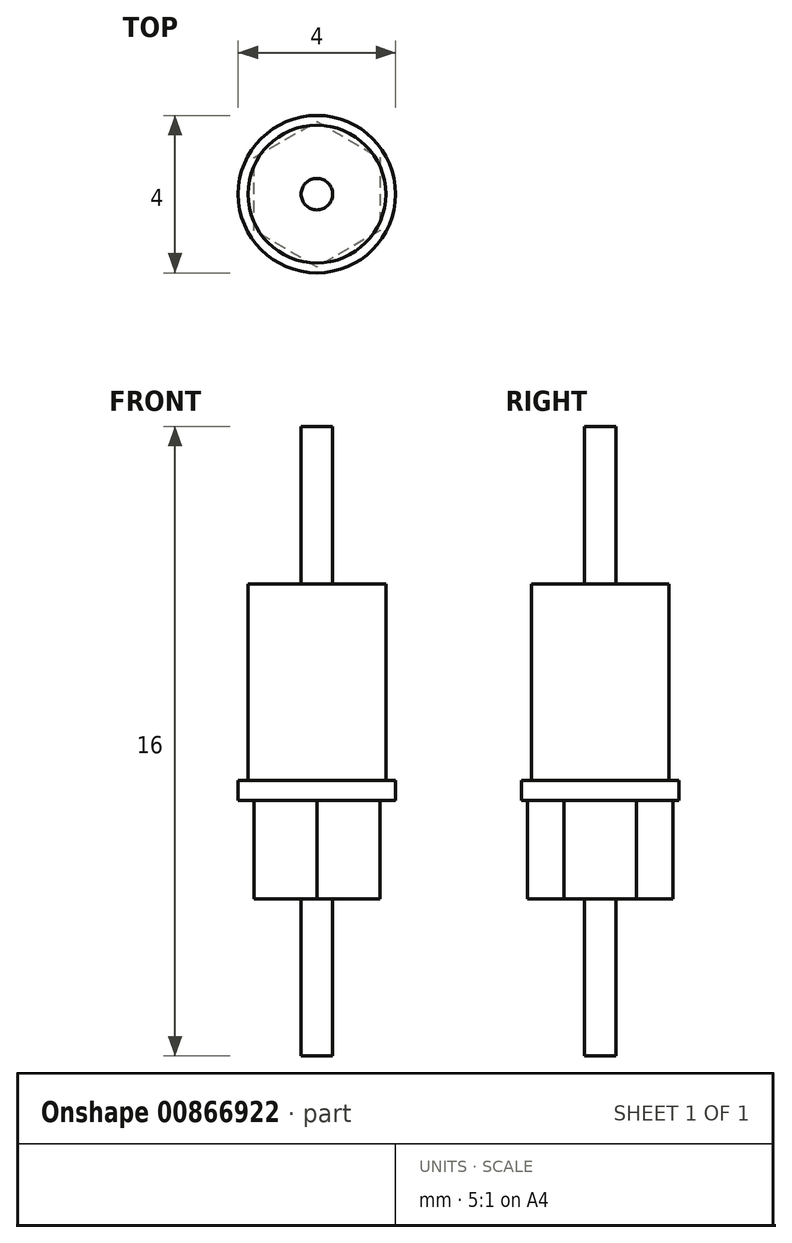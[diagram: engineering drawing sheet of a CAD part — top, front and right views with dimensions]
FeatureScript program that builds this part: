
annotation { "Feature Type Name" : "Feature", "Feature Type Description" : "" }
export const myFeature = defineFeature(function(context is Context, id is Id, definition is map)
    precondition{}
    {
        {
            var Q0;
            Q0=qCreatedBy(makeId("Top.planeOp"),FACE);
            var sketch = newSketch(context, id + "F0", { "sketchPlane" : qUnion([Q0])});
            skCircle(sketch, "E0", {"center": v(0, 0) * mm, "radius": 0.4 * mm});
            skSolve(sketch);
        }
        {
            var Q0;
            Q0=makeQuery(id+"F0.imprint","IMPRINT",FACE,{"disambiguationData":[TD([[makeQuery(id+"F0.imprint","IMPRINT",EDGE,{"derivedFrom":sQuery(id+"F0.wireOp",EDGE,"E0")}),1.0]])]});
            extrude(context, id + "F1", {"entities" : qUnion([Q0]), "depth" : 4 * mm, "offsetDistance" : 25 * mm});
        }
        {
            var Q0;
            Q0=makeQuery(id+"F1.opExtrude","CAP_FACE",FACE,{"disambiguationData":[OSD([sQuery(id+"F0.wireOp",EDGE,"E0")])],"isStart":false});
            var sketch = newSketch(context, id + "F2", { "sketchPlane" : qUnion([Q0])});
            skCircle(sketch, "E1.cCircle", {"center": v(0, 0) * mm, "radius": 1.6 * mm, "construction": true});
            skLineSegment(sketch, "E1.0", {"start": v(1.6, 0.92) * mm, "end": v(1.6, -0.92) * mm});
            skLineSegment(sketch, "E1.1", {"start": v(1.6, -0.92) * mm, "end": v(0, -1.85) * mm});
            skLineSegment(sketch, "E1.2", {"start": v(0, -1.85) * mm, "end": v(-1.6, -0.92) * mm});
            skLineSegment(sketch, "E1.3", {"start": v(-1.6, -0.92) * mm, "end": v(-1.6, 0.92) * mm});
            skLineSegment(sketch, "E1.4", {"start": v(-1.6, 0.92) * mm, "end": v(0, 1.85) * mm});
            skLineSegment(sketch, "E1.5", {"start": v(0, 1.85) * mm, "end": v(1.6, 0.92) * mm});
            skPoint(sketch, "E1.0.midPoint", {"position": v(1.6, 0) * mm});
            skSolve(sketch);
        }
        {
            var Q0;
            Q0=makeQuery(id+"F2.imprint","IMPRINT",FACE,{"disambiguationData":[TD([[makeQuery(id+"F2.imprint","IMPRINT",EDGE,{"derivedFrom":sQuery(id+"F2.wireOp",EDGE,"E1.0")}),-1.0]])]});
            var Q1;
            Q1=makeQuery(id+"F2.imprint","IMPRINT",FACE,{"disambiguationData":[TD([[makeQuery(id+"F2.imprint","IMPRINT",EDGE,{"derivedFrom":makeQuery(id+"F1.opExtrude","CAP_EDGE",EDGE,{"disambiguationData":[OSD([sQuery(id+"F0.wireOp",EDGE,"E0")])],"isStart":false})}),1.0]])]});
            extrude(context, id + "F3", {"entities" : qUnion([Q0, Q1]), "operationType" : NewBodyOperationType.ADD, "depth" : 2.5 * mm, "offsetDistance" : 25 * mm});
        }
        {
            var Q0;
            Q0=makeQuery(id+"F3.opExtrude","CAP_FACE",FACE,{"disambiguationData":[OSD([sQuery(id+"F0.wireOp",EDGE,"E0"),sQuery(id+"F2.wireOp",EDGE,"E1.0"),sQuery(id+"F2.wireOp",EDGE,"E1.1"),sQuery(id+"F2.wireOp",EDGE,"E1.2"),sQuery(id+"F2.wireOp",EDGE,"E1.3"),sQuery(id+"F2.wireOp",EDGE,"E1.4"),sQuery(id+"F2.wireOp",EDGE,"E1.5")])],"isStart":false});
            var sketch = newSketch(context, id + "F4", { "sketchPlane" : qUnion([Q0])});
            skCircle(sketch, "E2", {"center": v(0, 0) * mm, "radius": 2 * mm});
            skSolve(sketch);
        }
        {
            var Q0;
            Q0=makeQuery(id+"F4.imprint","IMPRINT",FACE,{"disambiguationData":[TD([[makeQuery(id+"F4.imprint","IMPRINT",EDGE,{"derivedFrom":sQuery(id+"F4.wireOp",EDGE,"E2")}),1.0]])]});
            var Q1;
            Q1=makeQuery(id+"F4.imprint","IMPRINT",FACE,{"disambiguationData":[TD([[makeQuery(id+"F4.imprint","IMPRINT",EDGE,{"derivedFrom":makeQuery(id+"F3.opExtrude","CAP_EDGE",EDGE,{"disambiguationData":[OSD([sQuery(id+"F2.wireOp",EDGE,"E1.0")])],"isStart":false})}),-1.0]])]});
            extrude(context, id + "F5", {"entities" : qUnion([Q0, Q1]), "operationType" : NewBodyOperationType.ADD, "depth" : 0.5 * mm, "offsetDistance" : 25 * mm});
        }
        {
            var Q0;
            Q0=makeQuery(id+"F5.opExtrude","CAP_FACE",FACE,{"disambiguationData":[OSD([sQuery(id+"F4.wireOp",EDGE,"E2")])],"isStart":false});
            var sketch = newSketch(context, id + "F6", { "sketchPlane" : qUnion([Q0])});
            skCircle(sketch, "E3", {"center": v(0, 0) * mm, "radius": 1.75 * mm});
            skSolve(sketch);
        }
        {
            var Q0;
            Q0=makeQuery(id+"F6.imprint","IMPRINT",FACE,{"disambiguationData":[TD([[makeQuery(id+"F6.imprint","IMPRINT",EDGE,{"derivedFrom":sQuery(id+"F6.wireOp",EDGE,"E3")}),1.0]])]});
            extrude(context, id + "F7", {"entities" : qUnion([Q0]), "operationType" : NewBodyOperationType.ADD, "depth" : 5 * mm, "offsetDistance" : 25 * mm});
        }
        {
            var Q0;
            Q0=makeQuery(id+"F7.opExtrude","CAP_FACE",FACE,{"disambiguationData":[OSD([sQuery(id+"F6.wireOp",EDGE,"E3")])],"isStart":false});
            var sketch = newSketch(context, id + "F8", { "sketchPlane" : qUnion([Q0])});
            skCircle(sketch, "E4", {"center": v(0, 0) * mm, "radius": 0.4 * mm});
            skSolve(sketch);
        }
        {
            var Q0;
            Q0 = qSketchRegion(id + "F8", true);
            extrude(context, id + "F9", {"entities" : qUnion([Q0]), "operationType" : NewBodyOperationType.ADD, "depth" : 4 * mm, "offsetDistance" : 25 * mm});
        }
    });
